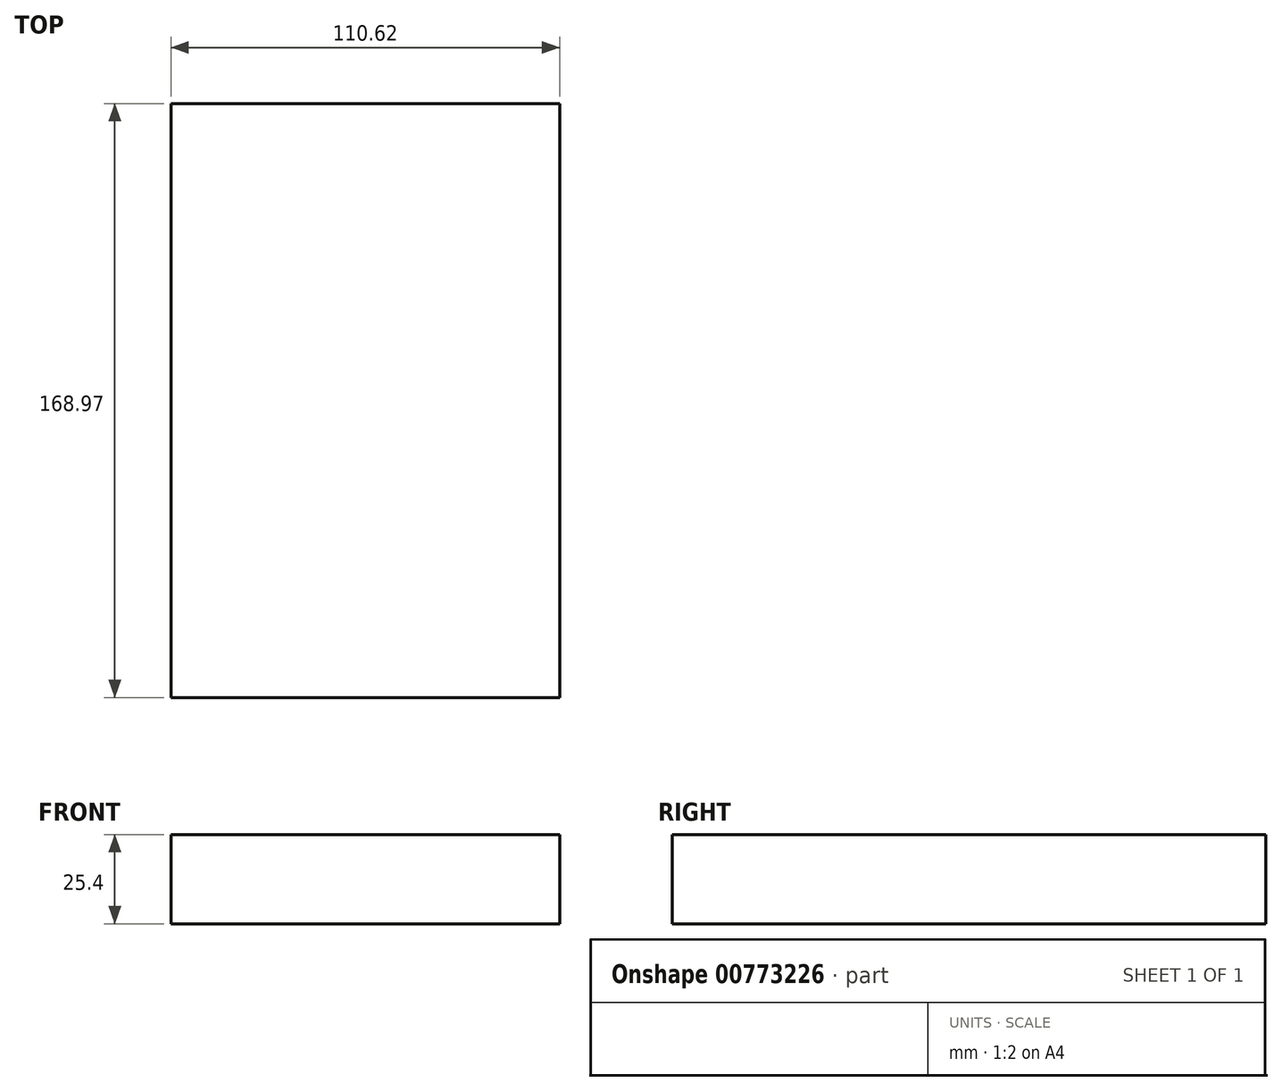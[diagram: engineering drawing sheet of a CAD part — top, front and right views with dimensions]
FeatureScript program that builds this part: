
annotation { "Feature Type Name" : "Feature", "Feature Type Description" : "" }
export const myFeature = defineFeature(function(context is Context, id is Id, definition is map)
    precondition{}
    {
        {
            var Q0;
            Q0=qCreatedBy(makeId("Top.planeOp"),FACE);
            var sketch = newSketch(context, id + "F0", { "sketchPlane" : qUnion([Q0])});
            skLineSegment(sketch, "E0.bottom", {"start": v(0, 0) * mm, "end": v(110.62, 0) * mm});
            skLineSegment(sketch, "E0.top", {"start": v(0, 168.97) * mm, "end": v(110.62, 168.97) * mm});
            skLineSegment(sketch, "E0.left", {"start": v(0, 0) * mm, "end": v(0, 168.97) * mm});
            skLineSegment(sketch, "E0.right", {"start": v(110.62, 0) * mm, "end": v(110.62, 168.97) * mm});
            skSolve(sketch);
        }
        {
            var Q0;
            Q0=qSketchRegion(id+"F0",true);
            extrude(context, id + "F1", {"entities" : qUnion([Q0]), "oppositeDirection" : true, "depth" : 25.4 * mm, "offsetDistance" : 25.4 * mm});
        }
    });
